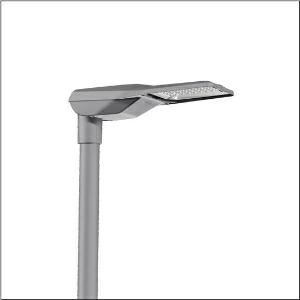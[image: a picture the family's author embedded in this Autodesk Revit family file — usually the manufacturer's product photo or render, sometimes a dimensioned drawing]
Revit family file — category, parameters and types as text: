
# Revit family: streetlight_sl_21_iq_mini___st1_0a_5xe2d31g08gb_f91a
name_source: partatom
category: Lighting Fixtures
units: mm (PartAtom-declared; Revit-internal decimal feet)

## family parameters
Cut with Voids When Loaded = No
Host = Face
Light Source = No
Part Type = Normal
Room Calculation Point = No
Round Connector Dimension = Use Diameter
Shared = No

## types (1)
- --- (1 x LED, 5680 lm, 37.1 W, 3000K)
    Apparent Load = 37 VA
    CIE Flux Codes = 37 72 97 100 100
    Color Rendering = 70
    Color Temperature = 3000K
    Default Elevation = 1800 mm
    Description = Streetlight SL 21 iQ mini, mast luminaire, primary light control with lens, of PMMA, primary optical cover: cover, of toughened safety glass, transparent, light distribution: ST1.0a, light emission: direct distribution, primary light characteristic: asymmetric, installation type: post-top, side-entry, LED, High Power LED, rated luminous flux: 5.680lm, luminous efficacy: 153lm/W, light colour: 730, colour temperature: 3000K, control: Street-Remote, Auto-Match, Temp-Guard, Lumen-Switch, Night-Set, Smart-Wire, Light-Fading, Desk-Remote (wireless, voltage-free reading and setting of iQ features in the workshop via application-optimized NFC function/RFID function), optimised constant luminous flux control (CLO 2.0), presetting dimming linear, mains connection: 220..240V, AC, 50/60Hz, start of lifetime: 37W, end of service life: 39W, reduction: 18W, luminaire housing, of diecast aluminium, powder-coated, Siteco® metallic grey (DB 702S), corrosivity category C5 mid according to DIN EN ISO 12944, please order mast flange separately, inclination adjustable: 0°, 5°, 10°, 15°, sealing non-destructively replaceable, multi-level sealing system, length: 628mm, width: 235mm, height: 110mm, mast flange for spigot size: 42mm (side-entry): 5XC10008XM4, 60/48mm (side-entry/post-top): 5XC10108XM2, 76/60mm (side-entry/post-top): 5XC10108XM1, protection rating (complete): IP66, insulation class (complete): insulation class II (safety insulation), certification: CE, ENEC, ENEC+, VDE, impact resistance: IK09, permissible operating ambient temperature for outdoor applications: -40..+50°C, standard-compliant lighting for roads and squares, packaging unit: 1 piece

Light Distribution: ST1.0a
    Height = 110 mm
    Lamp = 1 x LED
    Lamp Light Flux = 5680 lm
    Lamp Power = 37.1 W
    Lamp count = 1
    Length = 625 mm
    Luminous efficacy = 153 lm/W
    Manufacturer = Siteco
    ModVariant = No
    Model = 5XE2D31G08GB
    Number of Poles = 1
    OnlyDefault = Yes
    Power Factor = 1
    Product Name = Streetlight SL 21 iQ mini | ST1.0a
    Product group = mast luminaire | pylon top
    ProductGroupID = 6100
    Protection Class = Protection class II
    Protection Degree = IP 66
    RLX_Detail_Level = 1
    RLX_Emergency_Light_Flux = 0 lm
    RLX_Emergency_Type = 0
    RLX_Emergency_Type_DB = No
    RlxData = <blob elided: 92061 chars, md5=85141f93>
    Socket = socket
    Standby Power = 0 W
    System Light Flux = 5680 lm
    System Power = 37 W
    Type Comments = factory setting: luminous flux: 100 % | dim-lin: 254 | 385 mA
    Type Image = l_1003519.jpg
    URL = http://relux.com
    VarID = @adj_140975
    Voltage = 0 V
    Weight = 0.00 kg
    Width = 234 mm

## geometry (parser evidence)
native form markers: Blend x4, Sweep x10
no freeform markers — native parametric forms only
